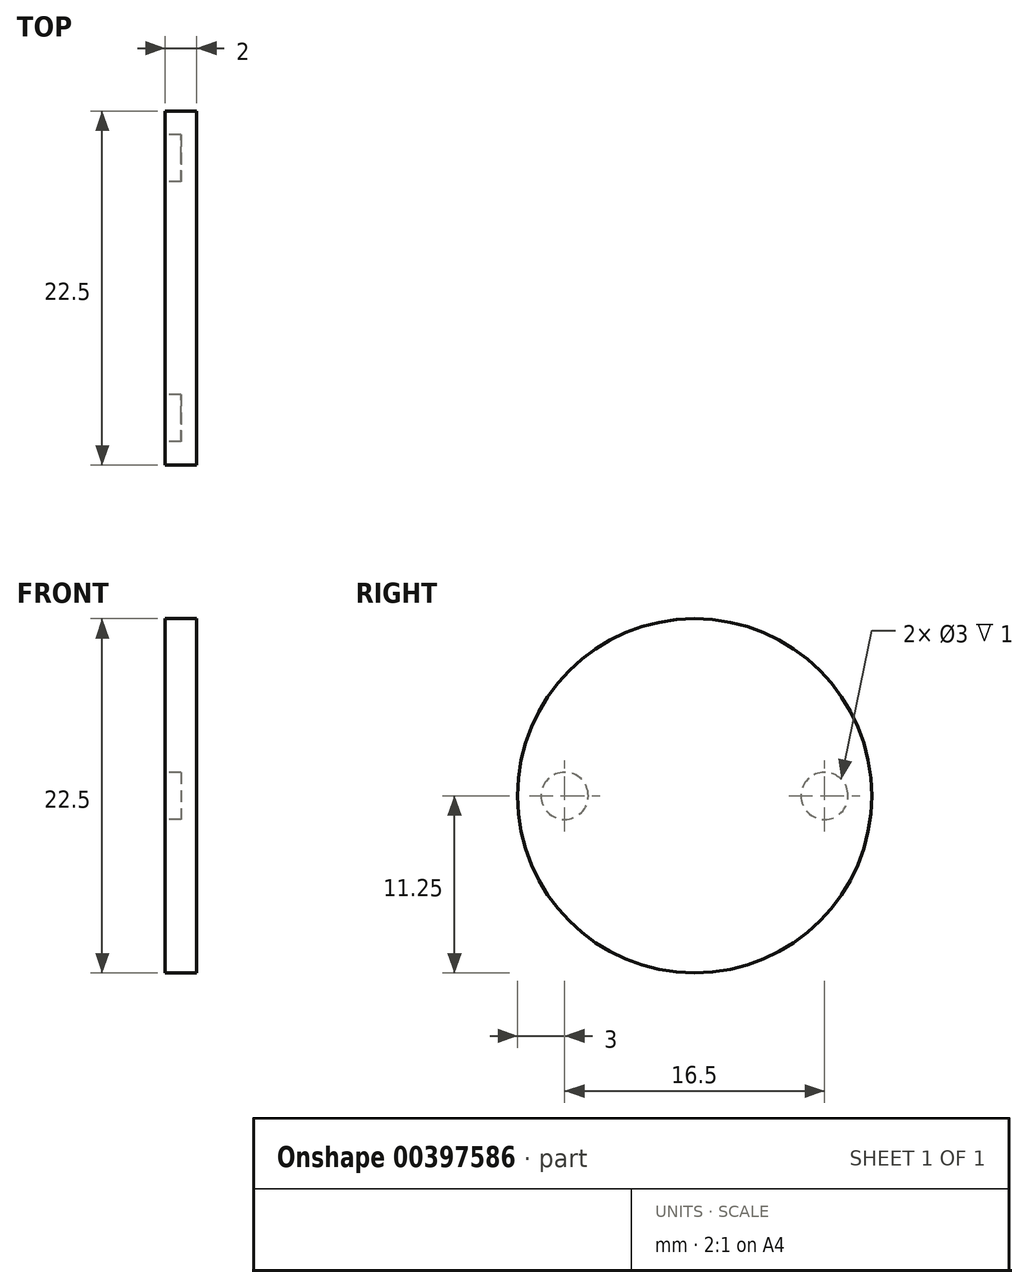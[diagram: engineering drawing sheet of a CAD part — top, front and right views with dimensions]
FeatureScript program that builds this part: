
annotation { "Feature Type Name" : "Feature", "Feature Type Description" : "" }
export const myFeature = defineFeature(function(context is Context, id is Id, definition is map)
    precondition{}
    {
        {
            var Q0;
            Q0=qCreatedBy(makeId("Right.planeOp"),FACE);
            var sketch = newSketch(context, id + "F0", { "sketchPlane" : qUnion([Q0])});
            skCircle(sketch, "E0", {"center": v(0, 0) * mm, "radius": 11.25 * mm});
            skSolve(sketch);
        }
        {
            var Q0;
            Q0=qSketchRegion(id+"F0",true);
            extrude(context, id + "F1", {"entities" : qUnion([Q0]), "depth" : 2 * mm});
        }
        {
            var Q0;
            Q0=makeQuery(id+"F1.opExtrude","CAP_FACE",FACE,{"disambiguationData":[OSD([sQuery(id+"F0.wireOp",EDGE,"E0")])],"isStart":true});
            var sketch = newSketch(context, id + "F2", { "sketchPlane" : qUnion([Q0])});
            skLineSegment(sketch, "E1", {"start": v(-11.25, 0) * mm, "end": v(11.25, 0) * mm});
            skLineSegment(sketch, "E2", {"start": v(-11.25, 0) * mm, "end": v(-8.25, 0) * mm});
            skLineSegment(sketch, "E3", {"start": v(11.25, 0) * mm, "end": v(8.25, 0) * mm});
            skCircle(sketch, "E4", {"center": v(-8.25, 0) * mm, "radius": 1.5 * mm});
            skCircle(sketch, "E5", {"center": v(8.25, 0) * mm, "radius": 1.5 * mm});
            skSolve(sketch);
        }
        {
            var Q0;
            Q0=qSketchRegion(id+"F2",true);
            extrude(context, id + "F3", {"entities" : qUnion([Q0]), "operationType" : NewBodyOperationType.REMOVE, "oppositeDirection" : true, "depth" : 1 * mm});
        }
    });
